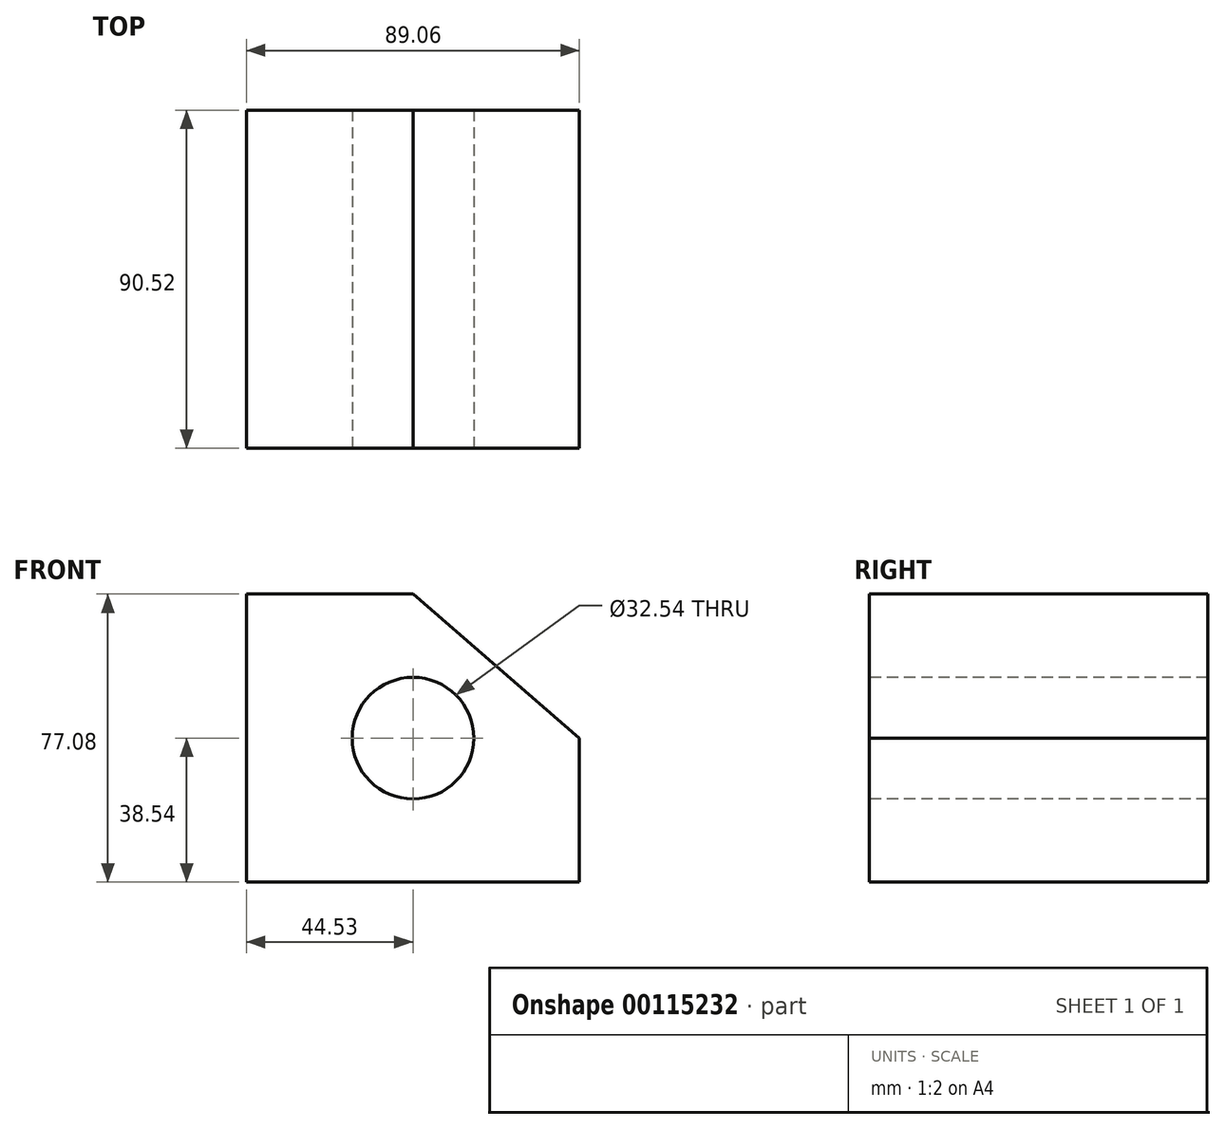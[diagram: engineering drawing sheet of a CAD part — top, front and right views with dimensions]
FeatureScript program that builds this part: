
annotation { "Feature Type Name" : "Feature", "Feature Type Description" : "" }
export const myFeature = defineFeature(function(context is Context, id is Id, definition is map)
    precondition{}
    {
        {
            var Q0;
            Q0=qCreatedBy(makeId("Front.planeOp"),FACE);
            var sketch = newSketch(context, id + "F0", { "sketchPlane" : qUnion([Q0])});
            skLineSegment(sketch, "E0.bottom", {"start": v(-44.53, 38.54) * mm, "end": v(44.53, 38.54) * mm});
            skLineSegment(sketch, "E0.top", {"start": v(-44.53, -38.54) * mm, "end": v(44.53, -38.54) * mm});
            skLineSegment(sketch, "E0.left", {"start": v(-44.53, 38.54) * mm, "end": v(-44.53, -38.54) * mm});
            skLineSegment(sketch, "E0.right", {"start": v(44.53, 38.54) * mm, "end": v(44.53, -38.54) * mm});
            skPoint(sketch, "E0.middle", {"position": v(0, 0) * mm});
            skSolve(sketch);
        }
        {
            var Q0;
            Q0=makeQuery(id+"F0.imprint","IMPRINT",FACE,{"disambiguationData":[TD([[makeQuery(id+"F0.imprint","IMPRINT",EDGE,{"derivedFrom":sQuery(id+"F0.wireOp",EDGE,"E0.bottom")}),-1.0]])]});
            extrude(context, id + "F1", {"entities" : qUnion([Q0]), "endBound" : BoundingType.SYMMETRIC, "depth" : 90.52 * mm});
        }
        {
            var Q0;
            Q0=makeQuery(id+"F1.opExtrude","CAP_FACE",FACE,{"disambiguationData":[OSD([sQuery(id+"F0.wireOp",EDGE,"E0.bottom"),sQuery(id+"F0.wireOp",EDGE,"E0.top"),sQuery(id+"F0.wireOp",EDGE,"E0.left"),sQuery(id+"F0.wireOp",EDGE,"E0.right")])],"isStart":false});
            var sketch = newSketch(context, id + "F2", { "sketchPlane" : qUnion([Q0])});
            skLineSegment(sketch, "E1", {"start": v(0, 38.54) * mm, "end": v(44.53, 0) * mm});
            skLineSegment(sketch, "E2", {"start": v(44.53, 0) * mm, "end": v(44.53, 38.54) * mm});
            skLineSegment(sketch, "E3", {"start": v(44.53, 38.54) * mm, "end": v(0, 38.54) * mm});
            skSolve(sketch);
        }
        {
            var Q0;
            Q0 = qSketchRegion(id + "F2", true);
            extrude(context, id + "F3", {"entities" : qUnion([Q0]), "operationType" : NewBodyOperationType.REMOVE, "endBound" : BoundingType.THROUGH_ALL, "oppositeDirection" : true, "depth" : 25.4 * mm});
        }
        {
            var Q0;
            Q0=qCreatedBy(makeId("Front.planeOp"),FACE);
            var sketch = newSketch(context, id + "F4", { "sketchPlane" : qUnion([Q0])});
            skCircle(sketch, "E4", {"center": v(0, 0) * mm, "radius": 16.27 * mm});
            skSolve(sketch);
        }
        {
            var Q0;
            Q0 = qSketchRegion(id + "F4", true);
            extrude(context, id + "F5", {"entities" : qUnion([Q0]), "operationType" : NewBodyOperationType.REMOVE, "endBound" : BoundingType.SYMMETRIC, "oppositeDirection" : true, "depth" : 92.2 * mm});
        }
    });
